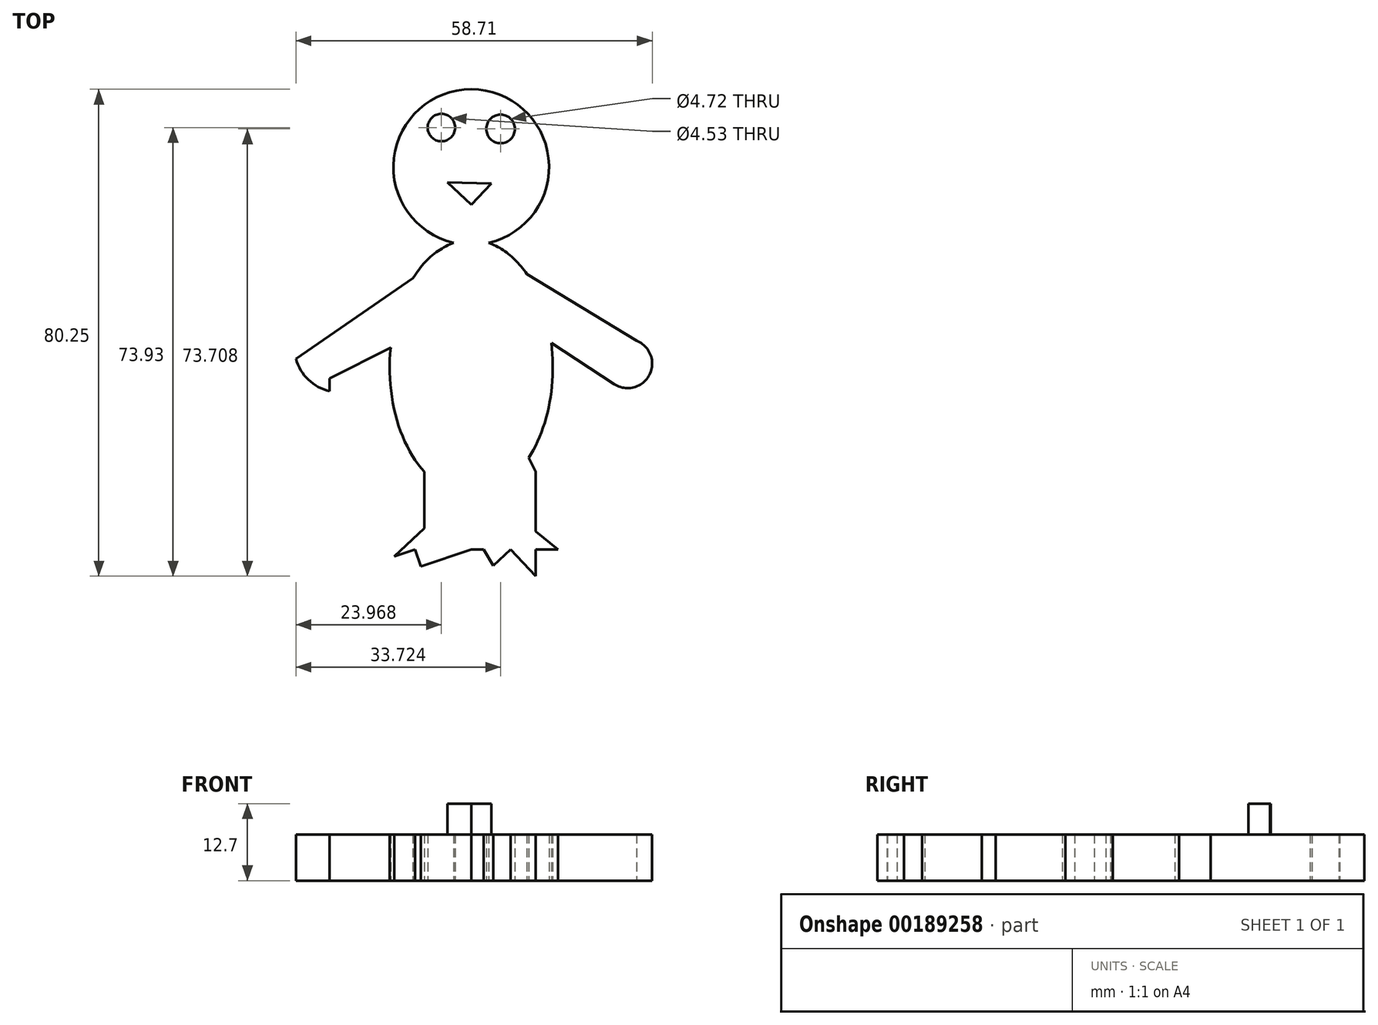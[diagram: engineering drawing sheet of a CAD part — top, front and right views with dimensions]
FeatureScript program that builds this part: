
annotation { "Feature Type Name" : "Feature", "Feature Type Description" : "" }
export const myFeature = defineFeature(function(context is Context, id is Id, definition is map)
    precondition{}
    {
        {
            var Q0;
            Q0=qCreatedBy(makeId("Top.planeOp"),FACE);
            var sketch = newSketch(context, id + "F0", { "sketchPlane" : qUnion([Q0])});
            skCircle(sketch, "E0", {"center": v(0, 50.22) * mm, "radius": 12.83 * mm});
            skEllipse(sketch, "E1", {"center": v(0, 17.2) * mm, "majorRadius": 21.01 * mm, "minorRadius": 13.45 * mm, "majorAxis": v(0, -1)});
            skCircle(sketch, "E2", {"center": v(-4.91, 56.73) * mm, "radius": 2.26 * mm});
            skPoint(sketch, "E2.first.point", {"position": v(-7.16, 56.46) * mm});
            skPoint(sketch, "E2.second.point", {"position": v(-2.77, 56) * mm});
            skPoint(sketch, "E2.third.point", {"position": v(-3.93, 58.77) * mm});
            skCircle(sketch, "E3", {"center": v(4.84, 56.5) * mm, "radius": 2.36 * mm});
            skPoint(sketch, "E3.first.point", {"position": v(4.16, 58.77) * mm});
            skPoint(sketch, "E3.second.point", {"position": v(4.85, 54.15) * mm});
            skPoint(sketch, "E3.third.point", {"position": v(2.54, 56) * mm});
            skLineSegment(sketch, "E4", {"start": v(-9.64, 31.86) * mm, "end": v(-28.88, 18.6) * mm});
            skLineSegment(sketch, "E5", {"start": v(-13.29, 20.45) * mm, "end": v(-23.34, 15.36) * mm});
            skLineSegment(sketch, "E6", {"start": v(9.18, 32.56) * mm, "end": v(27.24, 21.59) * mm});
            skLineSegment(sketch, "E7", {"start": v(13.2, 21.21) * mm, "end": v(23.58, 14.44) * mm});
            skArc(sketch, "E8", {"start": v(-28.88, 18.6) * mm, "mid": v(-26.84, 15.18) * mm, "end": v(-23.34, 13.28) * mm});
            skArc(sketch, "E9", {"start": v(23.58, 14.44) * mm, "mid": v(29.38, 15.98) * mm, "end": v(27.24, 21.59) * mm});
            skLineSegment(sketch, "E10", {"start": v(-7.72, 0) * mm, "end": v(-7.72, -6.35) * mm});
            skLineSegment(sketch, "E11", {"start": v(0, -3.8) * mm, "end": v(0, -7.5) * mm});
            skPoint(sketch, "E11.endSnap0", {"position": v(0, -3.8) * mm});
            skLineSegment(sketch, "E12", {"start": v(-7.72, -6.35) * mm, "end": v(-7.72, -9.35) * mm});
            skLineSegment(sketch, "E13", {"start": v(-7.72, -9.35) * mm, "end": v(-12.7, -13.97) * mm});
            skLineSegment(sketch, "E14", {"start": v(-12.7, -13.97) * mm, "end": v(-9.24, -12.82) * mm});
            skLineSegment(sketch, "E15", {"start": v(-9.24, -12.82) * mm, "end": v(-8.31, -15.59) * mm});
            skLineSegment(sketch, "E16", {"start": v(-8.31, -15.59) * mm, "end": v(0, -12.82) * mm});
            skLineSegment(sketch, "E17", {"start": v(0, -12.82) * mm, "end": v(2.3, -12.82) * mm});
            skLineSegment(sketch, "E18", {"start": v(2.3, -12.82) * mm, "end": v(0, -9.35) * mm});
            skLineSegment(sketch, "E19", {"start": v(10.62, 0) * mm, "end": v(10.62, -9.81) * mm});
            skLineSegment(sketch, "E20", {"start": v(10.62, -9.81) * mm, "end": v(14.32, -12.82) * mm});
            skLineSegment(sketch, "E21", {"start": v(14.32, -12.82) * mm, "end": v(10.62, -12.82) * mm});
            skLineSegment(sketch, "E22", {"start": v(10.62, -12.82) * mm, "end": v(10.62, -17.2) * mm});
            skLineSegment(sketch, "E23", {"start": v(10.62, -17.2) * mm, "end": v(6.47, -12.82) * mm});
            skLineSegment(sketch, "E24", {"start": v(6.47, -12.82) * mm, "end": v(3.62, -15.5) * mm});
            skLineSegment(sketch, "E25", {"start": v(3.62, -15.5) * mm, "end": v(0, -9.35) * mm});
            skLineSegment(sketch, "E26", {"start": v(-23.34, 13.28) * mm, "end": v(-23.34, 15.36) * mm});
            skLineSegment(sketch, "E27", {"start": v(10.62, 0) * mm, "end": v(9.47, 2.28) * mm});
            skSolve(sketch);
        }
        {
            var Q0;
            Q0=qCreatedBy(makeId("Top.planeOp"),FACE);
            var sketch = newSketch(context, id + "F1", { "sketchPlane" : qUnion([Q0])});
            skLineSegment(sketch, "E28", {"start": v(-3.93, 47.68) * mm, "end": v(0, 43.99) * mm});
            skLineSegment(sketch, "E29", {"start": v(0, 43.99) * mm, "end": v(3.34, 47.53) * mm});
            skLineSegment(sketch, "E30", {"start": v(-3.93, 47.68) * mm, "end": v(3.34, 47.53) * mm});
            skSolve(sketch);
        }
        {
            var Q0;
            Q0 = qSketchRegion(id + "F0", true);
            extrude(context, id + "F2", {"entities" : qUnion([Q0]), "depth" : 7.62 * mm});
        }
        {
            var Q0;
            Q0 = qSketchRegion(id + "F1", true);
            extrude(context, id + "F3", {"entities" : qUnion([Q0]), "operationType" : NewBodyOperationType.ADD, "depth" : 12.7 * mm});
        }
    });
